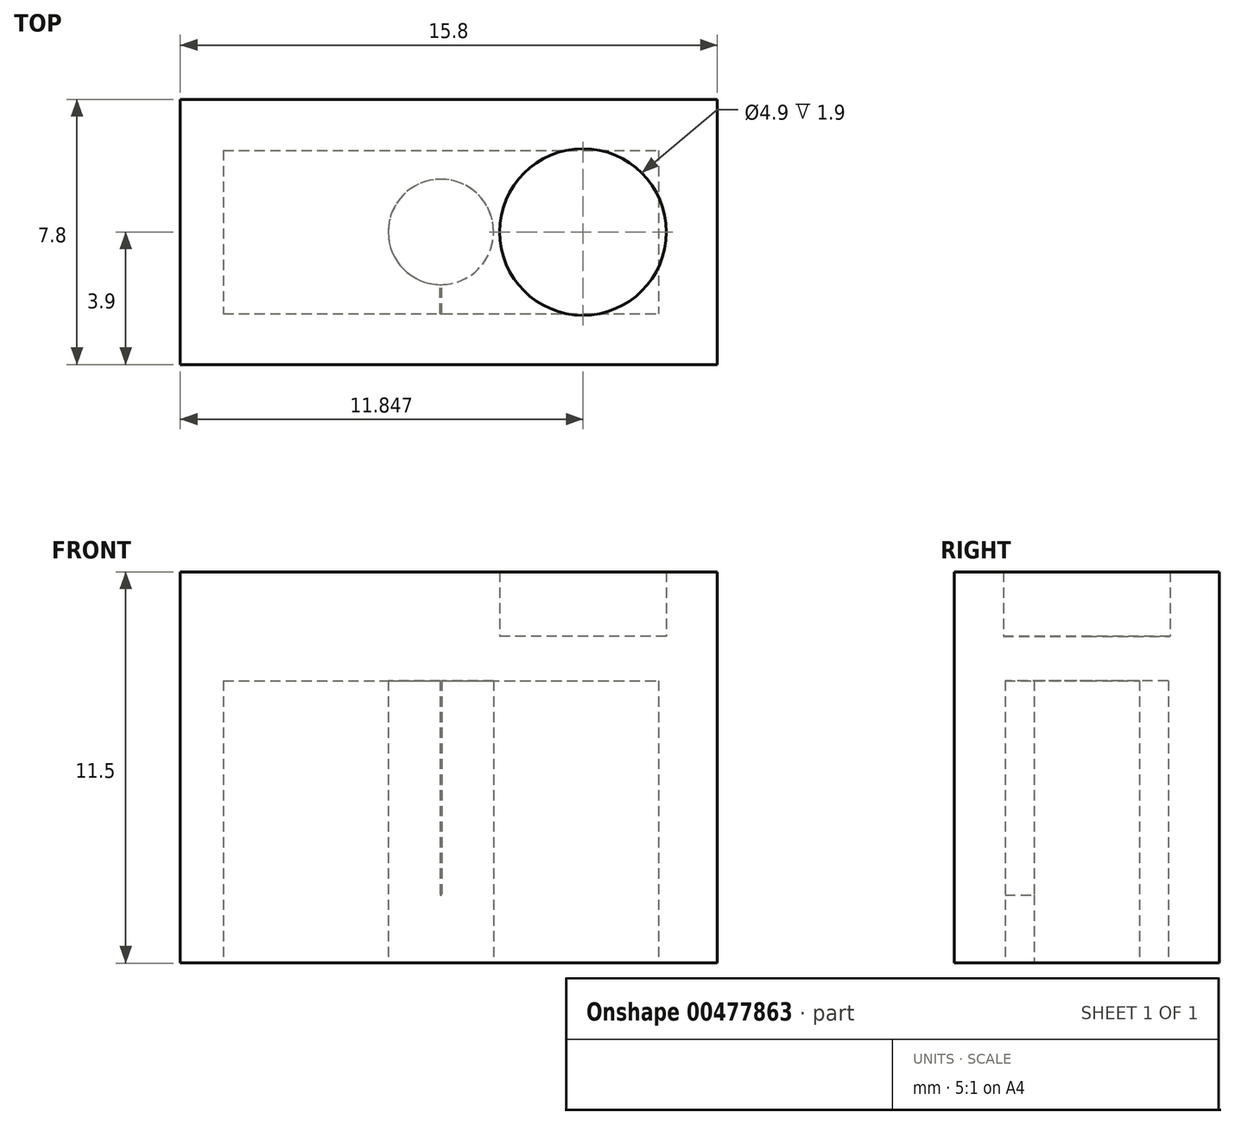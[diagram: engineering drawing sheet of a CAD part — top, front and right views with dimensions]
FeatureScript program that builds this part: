
annotation { "Feature Type Name" : "Feature", "Feature Type Description" : "" }
export const myFeature = defineFeature(function(context is Context, id is Id, definition is map)
    precondition{}
    {
        {
            var Q0;
            Q0=qCreatedBy(makeId("Front.planeOp"),FACE);
            var sketch = newSketch(context, id + "F0", { "sketchPlane" : qUnion([Q0])});
            skLineSegment(sketch, "E0", {"start": v(-54.55, -34.76) * mm, "end": v(-38.75, -34.76) * mm});
            skLineSegment(sketch, "E1", {"start": v(-38.75, -34.76) * mm, "end": v(-38.75, -25.16) * mm});
            skLineSegment(sketch, "E2", {"start": v(-38.75, -25.16) * mm, "end": v(-54.55, -25.16) * mm});
            skLineSegment(sketch, "E3", {"start": v(-54.55, -25.16) * mm, "end": v(-54.55, -34.76) * mm});
            skSolve(sketch);
        }
        {
            var Q0;
            Q0=makeQuery(id+"F0.imprint","IMPRINT",FACE,{"disambiguationData":[TD([[makeQuery(id+"F0.imprint","IMPRINT",EDGE,{"derivedFrom":sQuery(id+"F0.wireOp",EDGE,"E0")}),1.0]])]});
            extrude(context, id + "F1", {"entities" : qUnion([Q0]), "depth" : 7.8 * mm});
        }
        {
            var Q0;
            Q0=makeQuery(id+"F1.opExtrude","SWEPT_FACE",FACE,{"disambiguationData":[OSD([sQuery(id+"F0.wireOp",EDGE,"E2")])]});
            var sketch = newSketch(context, id + "F2", { "sketchPlane" : qUnion([Q0])});
            skCircle(sketch, "E4", {"center": v(-50.6, -3.9) * mm, "radius": 2.45 * mm});
            skCircle(sketch, "E5.MirrorC", {"center": v(-42.7, -3.9) * mm, "radius": 2.45 * mm});
            skSolve(sketch);
        }
        {
            var Q0;
            Q0=makeQuery(id+"F2.imprint","IMPRINT",FACE,{"disambiguationData":[TD([[makeQuery(id+"F2.imprint","IMPRINT",EDGE,{"derivedFrom":sQuery(id+"F2.wireOp",EDGE,"E4")}),1.0]])]});
            var Q1;
            Q1=makeQuery(id+"F2.imprint","IMPRINT",FACE,{"disambiguationData":[TD([[makeQuery(id+"F2.imprint","IMPRINT",EDGE,{"derivedFrom":sQuery(id+"F2.wireOp",EDGE,"E5.MirrorC")}),-1.0]])]});
            extrude(context, id + "F3", {"entities" : qUnion([Q0, Q1]), "operationType" : NewBodyOperationType.ADD, "depth" : 1.9 * mm});
        }
        {
            var Q0;
            Q0=makeQuery(id+"F1.opExtrude","SWEPT_FACE",FACE,{"disambiguationData":[OSD([sQuery(id+"F0.wireOp",EDGE,"E0")])]});
            var sketch = newSketch(context, id + "F4", { "sketchPlane" : qUnion([Q0])});
            skLineSegment(sketch, "E6.bottom", {"start": v(-53.28, 1.5) * mm, "end": v(-40.48, 1.5) * mm});
            skLineSegment(sketch, "E6.top", {"start": v(-53.28, 6.3) * mm, "end": v(-40.48, 6.3) * mm});
            skLineSegment(sketch, "E6.left", {"start": v(-53.28, 1.5) * mm, "end": v(-53.28, 6.3) * mm});
            skLineSegment(sketch, "E6.right", {"start": v(-40.48, 1.5) * mm, "end": v(-40.48, 6.3) * mm});
            skCircle(sketch, "E7", {"center": v(-46.88, 3.9) * mm, "radius": 1.55 * mm});
            skLineSegment(sketch, "E8", {"start": v(-46.88, 1.5) * mm, "end": v(-46.88, 2.35) * mm});
            skLineSegment(sketch, "E9", {"start": v(-46.88, 1.92) * mm, "end": v(-46.86, 1.92) * mm});
            skLineSegment(sketch, "E10", {"start": v(-46.86, 1.92) * mm, "end": v(-46.9, 1.92) * mm});
            skLineSegment(sketch, "E11", {"start": v(-46.86, 6.3) * mm, "end": v(-46.86, 5.45) * mm});
            skLineSegment(sketch, "E12", {"start": v(-46.9, 6.3) * mm, "end": v(-46.9, 5.45) * mm});
            skSolve(sketch);
        }
        {
            var Q0;
            Q0=makeQuery(id+"F4.imprint","IMPRINT",FACE,{"disambiguationData":[TD([[makeQuery(id+"F4.imprint","IMPRINT",EDGE,{"derivedFrom":sQuery(id+"F4.wireOp",EDGE,"E6.bottom")}),1.0]])]});
            extrude(context, id + "F5", {"entities" : qUnion([Q0]), "operationType" : NewBodyOperationType.REMOVE, "oppositeDirection" : true, "depth" : 8.3 * mm});
        }
        {
            var Q0;
            {var subQ0=sQuery(id+"F4.wireOp",EDGE,"E11");Q0=makeQuery(id+"F4.imprint","IMPRINT",FACE,{"disambiguationData":[TD([[makeQuery(id+"F4.imprint","IMPRINT",EDGE,{"derivedFrom":subQ0}),-1.0]])]});}
            extrude(context, id + "F6", {"entities" : qUnion([Q0]), "operationType" : NewBodyOperationType.REMOVE, "oppositeDirection" : true, "depth" : 2 * mm});
        }
    });
